# Revit family: FA_КронштейнДляМачтыТрубный_20_75717_EZETEK
name_source: partatom
category: Системы пожарной сигнализации
revit_build: Autodesk Revit 2017 (Build: 20170118_1100(x64)
units: mm (PartAtom-declared; Revit-internal decimal feet)

## family parameters
Всегда вертикально = Да
На основе рабочей плоскости = Нет
Общий = Да
При загрузке вырезать с полостями = Нет
Размер круглого соединителя = Использовать радиус
Сохранять ориентацию аннотаций = Нет
Тип детали = Нормальный
Точка расчета площади = Нет

## types (1)
- КронштейнДляМачтыТрубный_20_75717
    ADSK_Версия Revit = 2017
    ADSK_Единица измерения = шт.
    ADSK_Завод-изготовитель = Ezetek
    ADSK_Код изделия = 75717
    ADSK_Количество = 1
    ADSK_Марка = 75717
    ADSK_Масса = 0.55
    ADSK_Масса_Текст = 0.55
    ADSK_Материал = BIMLIB_Сталь_Нержавеющая_EZETEK
    ADSK_Наименование = Кронштейн для мачты 20 мм трубный, сталь
    ADSK_Обозначение = 75717
    URL = https://ezetek.ru
    Группа модели = Комплектующие для крепления мачт
    Изготовитель = Ezetek
    Описание = Кронштейн применяется для закрепления мачт типа СММ или СМЛ на элементы металлических конструкций. Диаметр мачты - от 32 до 63 мм, диаметр трубы - от 32 до 72 мм, просвет крепления 34 мм. Пластины кронштейна выполнены из окрашенной порошковым методом стали, не окрашенные детали оцинкованы.
    Угол = 90.00°
